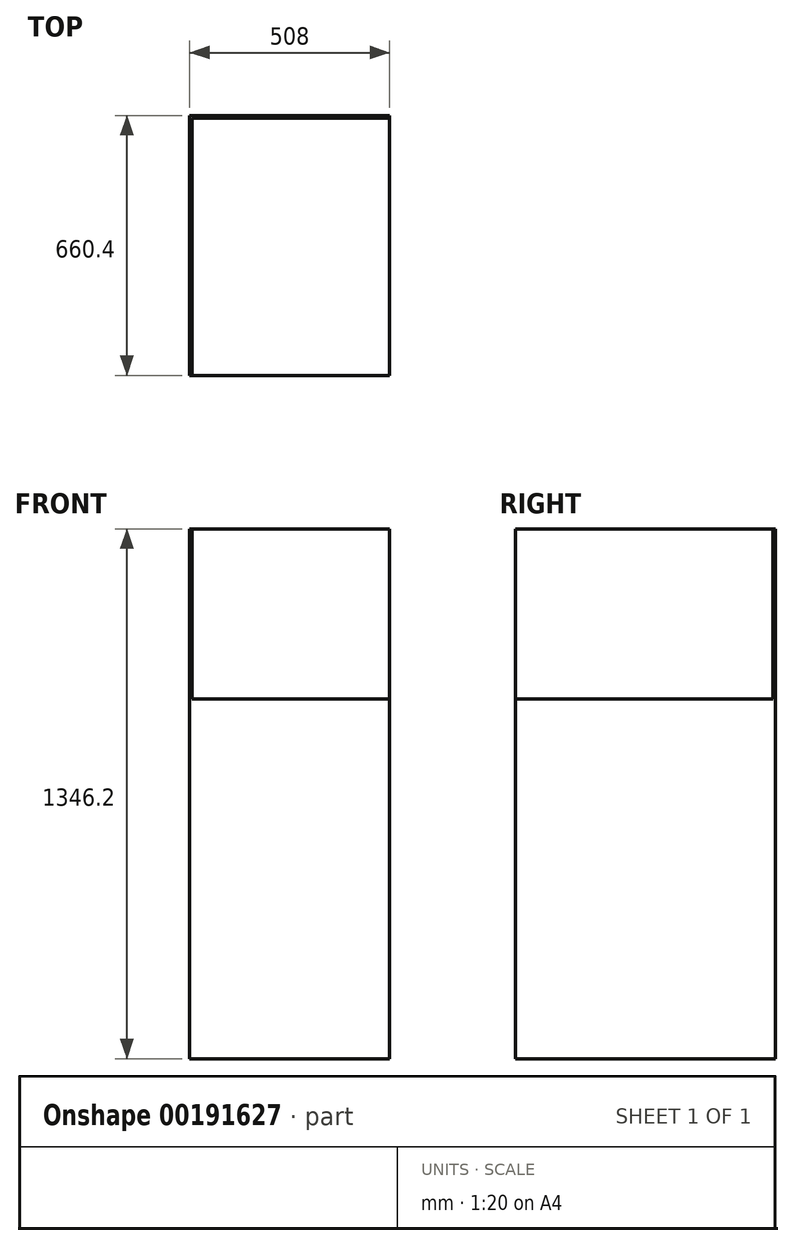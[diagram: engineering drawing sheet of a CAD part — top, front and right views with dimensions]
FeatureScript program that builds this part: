
annotation { "Feature Type Name" : "Feature", "Feature Type Description" : "" }
export const myFeature = defineFeature(function(context is Context, id is Id, definition is map)
    precondition{}
    {
        {
            var Q0;
            Q0=qCreatedBy(makeId("Top.planeOp"),FACE);
            var sketch = newSketch(context, id + "F0", { "sketchPlane" : qUnion([Q0])});
            skLineSegment(sketch, "E0.bottom", {"start": v(0, 0) * mm, "end": v(508, 0) * mm});
            skLineSegment(sketch, "E0.top", {"start": v(0, -660.4) * mm, "end": v(508, -660.4) * mm});
            skLineSegment(sketch, "E0.left", {"start": v(0, 0) * mm, "end": v(0, -660.4) * mm});
            skLineSegment(sketch, "E0.right", {"start": v(508, 0) * mm, "end": v(508, -660.4) * mm});
            skSolve(sketch);
        }
        {
            var Q0;
            Q0=makeQuery(id+"F0.imprint","IMPRINT",FACE,{"disambiguationData":[TD([[makeQuery(id+"F0.imprint","IMPRINT",EDGE,{"derivedFrom":sQuery(id+"F0.wireOp",EDGE,"E0.bottom")}),-1.0]])]});
            extrude(context, id + "F1", {"entities" : qUnion([Q0]), "depth" : 914.4 * mm});
        }
        {
            var Q0;
            Q0=makeQuery(id+"F1.opExtrude","CAP_FACE",FACE,{"disambiguationData":[OSD([sQuery(id+"F0.wireOp",EDGE,"E0.bottom"),sQuery(id+"F0.wireOp",EDGE,"E0.top"),sQuery(id+"F0.wireOp",EDGE,"E0.left"),sQuery(id+"F0.wireOp",EDGE,"E0.right")])],"isStart":false});
            var sketch = newSketch(context, id + "F2", { "sketchPlane" : qUnion([Q0])});
            skLineSegment(sketch, "E1.bottom", {"start": v(0, -660.4) * mm, "end": v(6.35, -660.4) * mm});
            skLineSegment(sketch, "E1.top", {"start": v(0, 0) * mm, "end": v(6.35, 0) * mm});
            skLineSegment(sketch, "E1.left", {"start": v(0, -660.4) * mm, "end": v(0, 0) * mm});
            skLineSegment(sketch, "E1.right", {"start": v(6.35, -660.4) * mm, "end": v(6.35, 0) * mm});
            skSolve(sketch);
        }
        {
            var Q0;
            Q0=makeQuery(id+"F2.imprint","IMPRINT",FACE,{"disambiguationData":[TD([[makeQuery(id+"F2.imprint","IMPRINT",EDGE,{"derivedFrom":sQuery(id+"F2.wireOp",EDGE,"E1.bottom")}),1.0]])]});
            extrude(context, id + "F3", {"entities" : qUnion([Q0]), "operationType" : NewBodyOperationType.ADD, "depth" : 431.8 * mm});
        }
        {
            var Q0;
            Q0=makeQuery(id+"F3.opExtrude","SWEPT_FACE",FACE,{"disambiguationData":[OSD([sQuery(id+"F2.wireOp",EDGE,"E1.right")])]});
            var sketch = newSketch(context, id + "F4", { "sketchPlane" : qUnion([Q0])});
            skLineSegment(sketch, "E2.bottom", {"start": v(0, 914.4) * mm, "end": v(-6.35, 914.4) * mm});
            skLineSegment(sketch, "E2.top", {"start": v(0, 1346.2) * mm, "end": v(-6.35, 1346.2) * mm});
            skLineSegment(sketch, "E2.left", {"start": v(0, 914.4) * mm, "end": v(0, 1346.2) * mm});
            skLineSegment(sketch, "E2.right", {"start": v(-6.35, 914.4) * mm, "end": v(-6.35, 1346.2) * mm});
            skSolve(sketch);
        }
        {
            var Q0;
            Q0=makeQuery(id+"F4.imprint","IMPRINT",FACE,{"disambiguationData":[TD([[makeQuery(id+"F4.imprint","IMPRINT",EDGE,{"derivedFrom":sQuery(id+"F4.wireOp",EDGE,"E2.bottom")}),1.0]])]});
            extrude(context, id + "F5", {"entities" : qUnion([Q0]), "operationType" : NewBodyOperationType.ADD, "depth" : 501.65 * mm});
        }
    });
